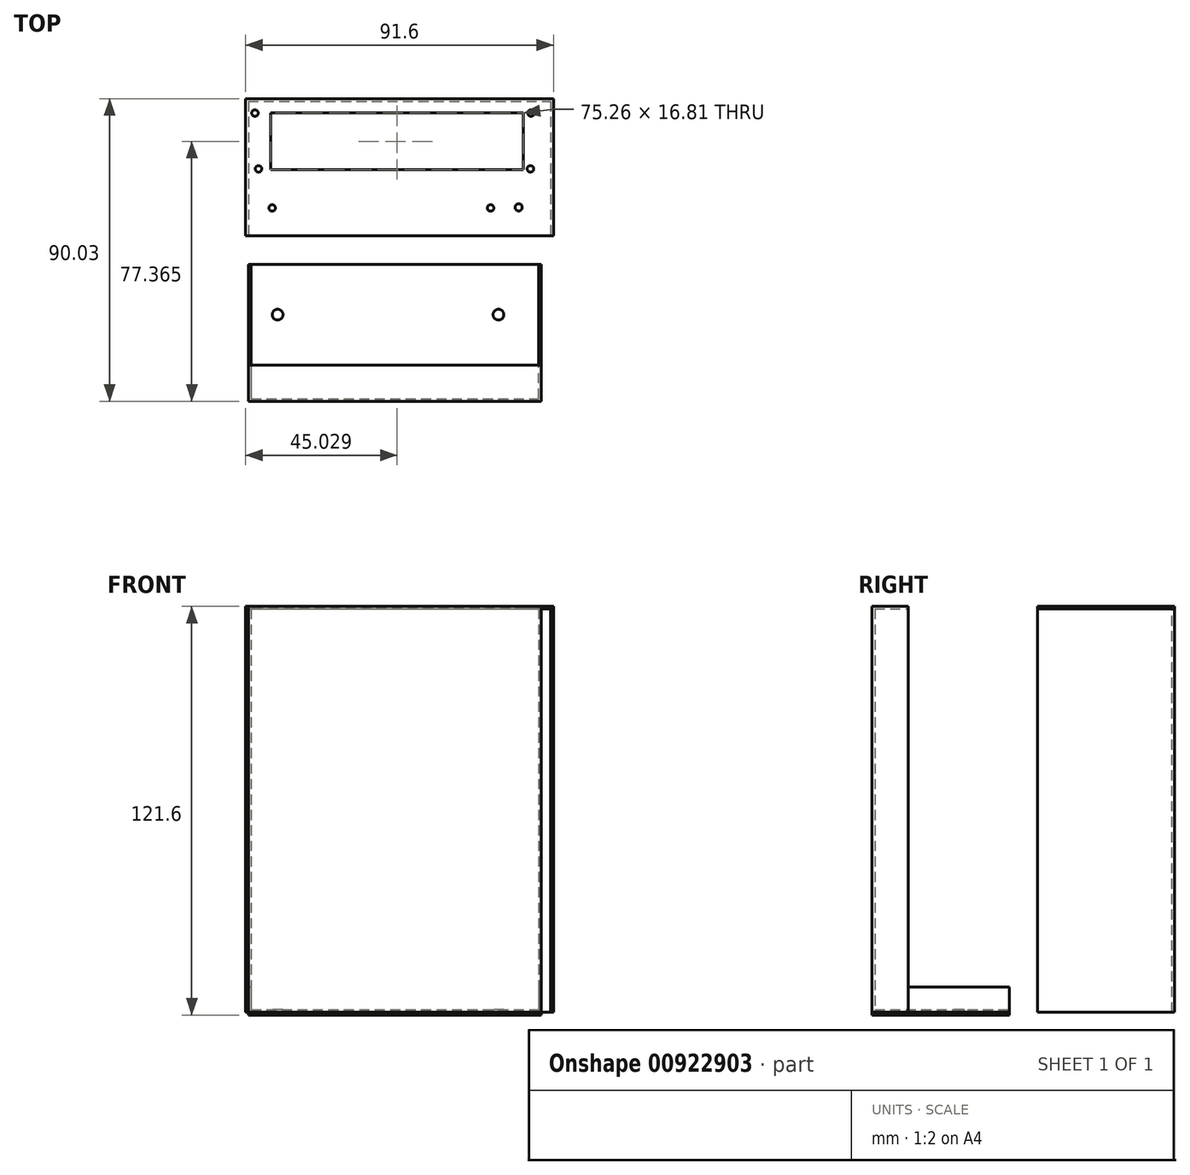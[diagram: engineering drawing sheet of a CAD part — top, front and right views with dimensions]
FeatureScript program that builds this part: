
annotation { "Feature Type Name" : "Feature", "Feature Type Description" : "" }
export const myFeature = defineFeature(function(context is Context, id is Id, definition is map)
    precondition{}
    {
        {
            var Q0;
            Q0=qCreatedBy(makeId("Top.planeOp"),FACE);
            var sketch = newSketch(context, id + "F0", { "sketchPlane" : qUnion([Q0])});
            skLineSegment(sketch, "E0.bottom", {"start": v(0, 0) * mm, "end": v(90, 0) * mm});
            skLineSegment(sketch, "E0.top", {"start": v(0, -40) * mm, "end": v(90, -40) * mm});
            skLineSegment(sketch, "E0.left", {"start": v(0, 0) * mm, "end": v(0, -40) * mm});
            skLineSegment(sketch, "E0.right", {"start": v(90, 0) * mm, "end": v(90, -40) * mm});
            skCircle(sketch, "E1", {"center": v(7.1, -31.7) * mm, "radius": 0.97 * mm});
            skCircle(sketch, "E2", {"center": v(1.95, -3.46) * mm, "radius": 0.97 * mm});
            skCircle(sketch, "E3", {"center": v(84.14, -3.46) * mm, "radius": 0.97 * mm});
            skCircle(sketch, "E4", {"center": v(83.96, -20.06) * mm, "radius": 0.97 * mm});
            skCircle(sketch, "E5", {"center": v(3.02, -20.06) * mm, "radius": 0.97 * mm});
            skLineSegment(sketch, "E6", {"start": v(0, -40) * mm, "end": v(-0.8, -40) * mm});
            skLineSegment(sketch, "E7", {"start": v(-0.8, -40) * mm, "end": v(-0.8, 0.8) * mm});
            skLineSegment(sketch, "E8", {"start": v(-0.8, 0.8) * mm, "end": v(90.8, 0.8) * mm});
            skLineSegment(sketch, "E9", {"start": v(90.8, 0.8) * mm, "end": v(90.8, -40) * mm});
            skLineSegment(sketch, "E10", {"start": v(90.8, -40) * mm, "end": v(90, -40) * mm});
            skCircle(sketch, "E11", {"center": v(72.1, -31.7) * mm, "radius": 0.97 * mm});
            skLineSegment(sketch, "E12.bottom", {"start": v(6.6, -3.46) * mm, "end": v(81.86, -3.46) * mm});
            skLineSegment(sketch, "E12.top", {"start": v(6.6, -20.27) * mm, "end": v(81.86, -20.27) * mm});
            skLineSegment(sketch, "E12.left", {"start": v(6.6, -3.46) * mm, "end": v(6.6, -20.27) * mm});
            skLineSegment(sketch, "E12.right", {"start": v(81.86, -3.46) * mm, "end": v(81.86, -20.27) * mm});
            skCircle(sketch, "E13", {"center": v(80.44, -31.52) * mm, "radius": 1.07 * mm});
            skSolve(sketch);
        }
        {
            var Q0;
            Q0=makeQuery(id+"F0.imprint","IMPRINT",FACE,{"disambiguationData":[TD([[makeQuery(id+"F0.imprint","IMPRINT",EDGE,{"derivedFrom":sQuery(id+"F0.wireOp",EDGE,"E0.bottom")}),1.0]])]});
            extrude(context, id + "F1", {"entities" : qUnion([Q0]), "oppositeDirection" : true, "depth" : 120 * mm, "offsetDistance" : 25 * mm});
        }
        {
            var Q0;
            Q0=makeQuery(id+"F0.imprint","IMPRINT",FACE,{"disambiguationData":[TD([[makeQuery(id+"F0.imprint","IMPRINT",EDGE,{"derivedFrom":sQuery(id+"F0.wireOp",EDGE,"E0.bottom")}),1.0]])]});
            var Q1;
            Q1=makeQuery(id+"F0.imprint","IMPRINT",FACE,{"disambiguationData":[TD([[makeQuery(id+"F0.imprint","IMPRINT",EDGE,{"derivedFrom":sQuery(id+"F0.wireOp",EDGE,"E0.bottom")}),-1.0]])]});
            extrude(context, id + "F2", {"entities" : qUnion([Q0, Q1]), "depth" : .8 * mm, "offsetDistance" : 25 * mm});
        }
        {
            var Q0;
            Q0=qCreatedBy(makeId("Top.planeOp"),FACE);
            cPlane(context, id + "F3", {"entities" : qUnion([Q0]), "cplaneType" : CPlaneType.OFFSET, "offset" : 120 * mm, "oppositeDirection" : true, "width" : 150 * mm, "height" : 150 * mm});
        }
        {
            var Q0;
            Q0=qCreatedBy(id+"F3.planeOp",FACE);
            var Q1;
            Q1=qCreatedBy(id+"F3.planeOp",FACE);
            var sketch = newSketch(context, id + "F4", { "sketchPlane" : qUnion([Q0, Q1])});
            skLineSegment(sketch, "E14.bottom", {"start": v(0, -48.43) * mm, "end": v(87.17, -48.43) * mm});
            skLineSegment(sketch, "E14.top", {"start": v(0, -89.23) * mm, "end": v(87.17, -89.23) * mm});
            skLineSegment(sketch, "E14.left", {"start": v(0, -48.43) * mm, "end": v(0, -89.23) * mm});
            skLineSegment(sketch, "E14.right", {"start": v(87.17, -48.43) * mm, "end": v(87.17, -89.23) * mm});
            skLineSegment(sketch, "E15", {"start": v(0, -78.43) * mm, "end": v(0.8, -78.43) * mm});
            skLineSegment(sketch, "E16", {"start": v(0.8, -78.43) * mm, "end": v(0.8, -88.43) * mm});
            skLineSegment(sketch, "E17", {"start": v(0.8, -88.43) * mm, "end": v(86.37, -88.43) * mm});
            skLineSegment(sketch, "E18", {"start": v(86.37, -88.43) * mm, "end": v(86.37, -78.43) * mm});
            skLineSegment(sketch, "E19", {"start": v(86.37, -78.43) * mm, "end": v(87.17, -78.43) * mm});
            skCircle(sketch, "E20", {"center": v(8.7, -63.43) * mm, "radius": 1.6 * mm});
            skCircle(sketch, "E21", {"center": v(74.44, -63.43) * mm, "radius": 1.6 * mm});
            skLineSegment(sketch, "E22", {"start": v(86.37, -78.43) * mm, "end": v(86.37, -48.43) * mm});
            skLineSegment(sketch, "E23", {"start": v(0.8, -78.43) * mm, "end": v(0.8, -48.43) * mm});
            skSolve(sketch);
        }
        {
            var Q0;
            {var subQ1=sQuery(id+"F4.wireOp",EDGE,"E14.top");Q0=makeQuery(id+"F4.imprint","IMPRINT",FACE,{"disambiguationData":[TD([[makeQuery(id+"F4.imprint","IMPRINT",EDGE,{"derivedFrom":subQ1}),1.0]])]});}
            var Q1;
            {var subQ2=sQuery(id+"F4.wireOp",EDGE,"E14.bottom");Q1=makeQuery(id+"F4.imprint","IMPRINT",FACE,{"disambiguationData":[TD([[makeQuery(id+"F4.imprint","IMPRINT",EDGE,{"derivedFrom":subQ2}),-1.0]])]});}
            extrude(context, id + "F5", {"entities" : qUnion([Q0, Q1]), "oppositeDirection" : true, "depth" : .8 * mm, "offsetDistance" : 25 * mm});
        }
        {
            var Q0;
            {var subQ1=sQuery(id+"F4.wireOp",EDGE,"E14.top");Q0=makeQuery(id+"F4.imprint","IMPRINT",FACE,{"disambiguationData":[TD([[makeQuery(id+"F4.imprint","IMPRINT",EDGE,{"derivedFrom":subQ1}),1.0]])]});}
            extrude(context, id + "F6", {"entities" : qUnion([Q0]), "depth" : 120 * mm, "offsetDistance" : 25 * mm});
        }
        {
            var Q0;
            {var subQ4=sQuery(id+"F4.wireOp",EDGE,"E19");Q0=makeQuery(id+"F4.imprint","IMPRINT",FACE,{"disambiguationData":[TD([[makeQuery(id+"F4.imprint","IMPRINT",EDGE,{"derivedFrom":subQ4}),1.0]])]});}
            var Q1;
            {var subQ4=sQuery(id+"F4.wireOp",EDGE,"E15");Q1=makeQuery(id+"F4.imprint","IMPRINT",FACE,{"disambiguationData":[TD([[makeQuery(id+"F4.imprint","IMPRINT",EDGE,{"derivedFrom":subQ4}),1.0]])]});}
            extrude(context, id + "F7", {"entities" : qUnion([Q0, Q1]), "depth" : 7.5 * mm, "offsetDistance" : 25 * mm});
        }
        {
            var Q0;
            Q0=makeQuery(id+"F6.opExtrude","CAP_FACE",FACE,{"disambiguationData":[OSD([sQuery(id+"F4.wireOp",EDGE,"E14.top"),sQuery(id+"F4.wireOp",EDGE,"E14.left"),sQuery(id+"F4.wireOp",EDGE,"E14.right"),sQuery(id+"F4.wireOp",EDGE,"E15"),sQuery(id+"F4.wireOp",EDGE,"E16"),sQuery(id+"F4.wireOp",EDGE,"E17"),sQuery(id+"F4.wireOp",EDGE,"E18"),sQuery(id+"F4.wireOp",EDGE,"E19")])],"isStart":false});
            var sketch = newSketch(context, id + "F8", { "sketchPlane" : qUnion([Q0])});
            skLineSegment(sketch, "E24.bottom", {"start": v(0, -89.23) * mm, "end": v(87.17, -89.23) * mm});
            skLineSegment(sketch, "E24.top", {"start": v(0, -78.43) * mm, "end": v(87.17, -78.43) * mm});
            skLineSegment(sketch, "E24.left", {"start": v(0, -89.23) * mm, "end": v(0, -78.43) * mm});
            skLineSegment(sketch, "E24.right", {"start": v(87.17, -89.23) * mm, "end": v(87.17, -78.43) * mm});
            skSolve(sketch);
        }
        {
            var Q0;
            Q0=makeQuery(id+"F8.imprint","IMPRINT",FACE,{"disambiguationData":[TD([[makeQuery(id+"F8.imprint","IMPRINT",EDGE,{"derivedFrom":sQuery(id+"F8.wireOp",EDGE,"E24.bottom")}),1.0]])]});
            var Q1;
            {var subQ1=makeQuery(id+"F6.opExtrude","CAP_EDGE",EDGE,{"disambiguationData":[OSD([sQuery(id+"F4.wireOp",EDGE,"E16")])],"isStart":false});Q1=makeQuery(id+"F8.imprint","IMPRINT",FACE,{"disambiguationData":[TD([[makeQuery(id+"F8.imprint","IMPRINT",EDGE,{"derivedFrom":subQ1}),1.0]])]});}
            extrude(context, id + "F9", {"entities" : qUnion([Q0, Q1]), "operationType" : NewBodyOperationType.ADD, "depth" : .8 * mm, "offsetDistance" : 25 * mm});
        }
        {
            var Q0;
            Q0=makeQuery(id+"F4.imprint","IMPRINT",FACE,{"disambiguationData":[TD([[makeQuery(id+"F4.imprint","IMPRINT",EDGE,{"derivedFrom":sQuery(id+"F4.wireOp",EDGE,"E16")}),1.0]])]});
            extrude(context, id + "F10", {"entities" : qUnion([Q0]), "depth" : .8 * mm, "offsetDistance" : 25 * mm});
        }
    });
